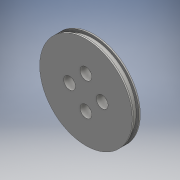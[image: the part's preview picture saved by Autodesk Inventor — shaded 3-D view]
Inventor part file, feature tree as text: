
AUTODESK INVENTOR PART (.ipt)
format: ipt  version: 2016 (Build 200138000, 138)  size: 125,952 bytes
history: native  units: mm
features: sketch x4, extrude x3, hole x1
ambient origin geometry x8: Origin, YZ Plane, XZ Plane, XY Plane, X Axis, Y Axis, Z Axis, Center Point
bodies: Solid1 (feature_tree)
feature tree (8):
  extrude  "Extrusion1"  Depth=0.5mm TaperAngle=0.0deg
  extrude  "Extrusion2"  Depth=2.0mm TaperAngle=0.0deg
  extrude  "Extrusion3"  Depth=0.5mm
  hole  "Hole1"  [1 undecoded]
  sketch  "Sketch1"  dims[d0=34.0mm d1=0.5mm d2=0.0mm]
  sketch  "Sketch2"  dims[d3=32.0mm d4=2.0mm d5=0.0mm]
  sketch  "Sketch3"  dims[d6=0.5mm d7=0.0mm d8=4.35mm]
  sketch  "Sketch4"  dims[d9=6.0mm d10=4.35mm d11=6.0mm d12=4.35mm d13=6.0mm d14=4.35mm d15=6.0mm d16=4.35mm d17=6.0mm d18=4.0mm d19=2.0mm d20=90.0deg d21=8.0mm d22=20.594885mm]
note: 1 required parameter value undecoded (feature->parameter linkage not recoverable at this tier; creation-order binding heuristic only, values carry confidence <= 0.55)
